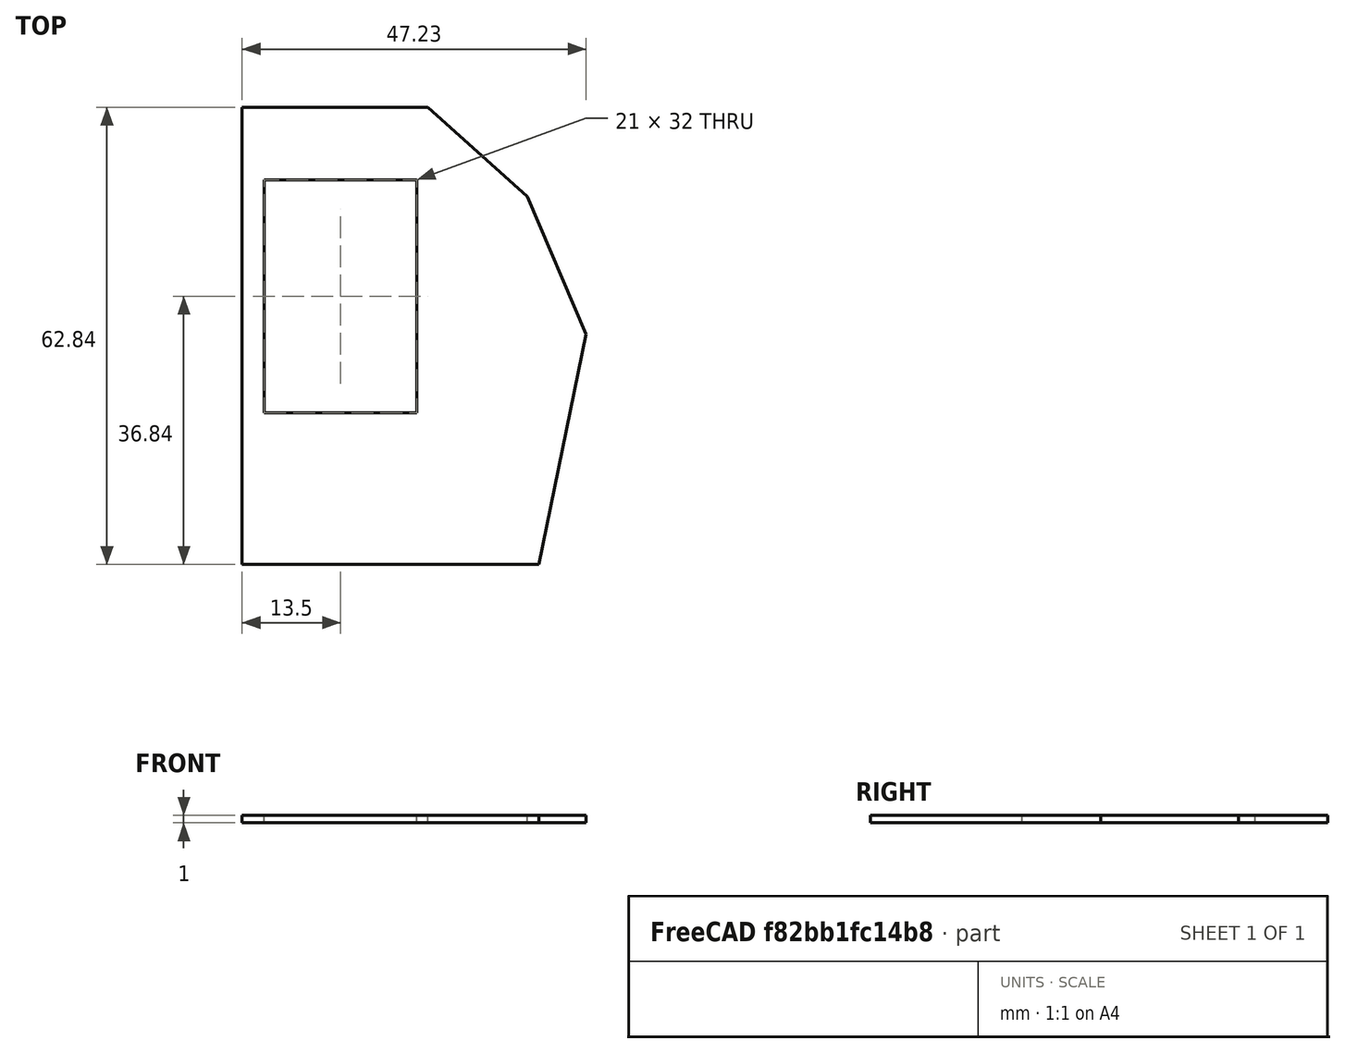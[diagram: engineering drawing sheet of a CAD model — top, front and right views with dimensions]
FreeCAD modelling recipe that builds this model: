
FCSTD DOCUMENT  (FreeCAD 0.19R24291 (Git))
Label: bottom-button
License: All rights reserved
LicenseURL: http://en.wikipedia.org/wiki/All_rights_reserved
objects: Sketcher::SketchObject×1, PartDesign::Pad×1, PartDesign::Body×1
note: 4 computed .brp shape members not serialized (recipe doc carries the construction recipe); baked Part::Feature solids carry a one-line shape summary decoded from their .brp

FEATURE [Sketcher::SketchObject] Sketch
  FullyConstrained = false
  MapMode = 5
  Support = -> [XY_Plane]
  sketch-geometry (10):
    g0: LineSegment StartX=-2.22 StartY=59.76 StartZ=0 EndX=-2.22 EndY=-3.08 EndZ=0
    g1: LineSegment StartX=-2.22 StartY=-3.08 StartZ=0 EndX=38.49 EndY=-3.08 EndZ=0
    g2: LineSegment StartX=38.49 StartY=-3.08 StartZ=0 EndX=45.01 EndY=28.5398 EndZ=0
    g3: LineSegment StartX=45.01 StartY=28.5398 StartZ=0 EndX=36.9087 EndY=47.5089 EndZ=0
    g4: LineSegment StartX=36.9087 StartY=47.5089 StartZ=0 EndX=23.2746 EndY=59.76 EndZ=0
    g5: LineSegment StartX=23.2746 StartY=59.76 StartZ=0 EndX=-2.22 EndY=59.76 EndZ=0
    g6: LineSegment StartX=0.78 StartY=49.76 StartZ=0 EndX=21.78 EndY=49.76 EndZ=0
    g7: LineSegment StartX=21.78 StartY=49.76 StartZ=0 EndX=21.78 EndY=17.76 EndZ=0
    g8: LineSegment StartX=21.78 StartY=17.76 StartZ=0 EndX=0.78 EndY=17.76 EndZ=0
    g9: LineSegment StartX=0.78 StartY=17.76 StartZ=0 EndX=0.78 EndY=49.76 EndZ=0
  constraints (25):
    c: Vertical(g0)
    c: Coincident(g0,g1)
    c: Horizontal(g1)
    c: Coincident(g1,g2)
    c: Coincident(g2,g3)
    c: Coincident(g3,g4)
    c: Coincident(g4,g5)
    c: Coincident(g5,g0)
    c: Horizontal(g5)
    c: DistanceY(g0,g-1) = 3.08
    c: DistanceY(g-1,g0) = 59.76
    c: DistanceX(g0,g-1) = 2.22
    c: DistanceX(g-1,g1) = 38.49
    c: Coincident(g6,g7)
    c: Coincident(g7,g8)
    c: Coincident(g8,g9)
    c: Coincident(g9,g6)
    c: Horizontal(g6)
    c: Horizontal(g8)
    c: Vertical(g7)
    c: Vertical(g9)
    c: DistanceX(g0,g6) = 3
    c: DistanceX(g0,g6) = 24
    c: DistanceY(g6,g0) = 10
    c: DistanceY(g8,g0) = 42
FEATURE [PartDesign::Pad] Pad
  Direction = (1,1,1)
  Length = 1
  Length2 = 100
  Profile = -> Sketch
  Type = 0
FEATURE [PartDesign::Body] Body
  Group = -> [Sketch,Pad]
  Origin = -> Origin
  Tip = -> Pad
